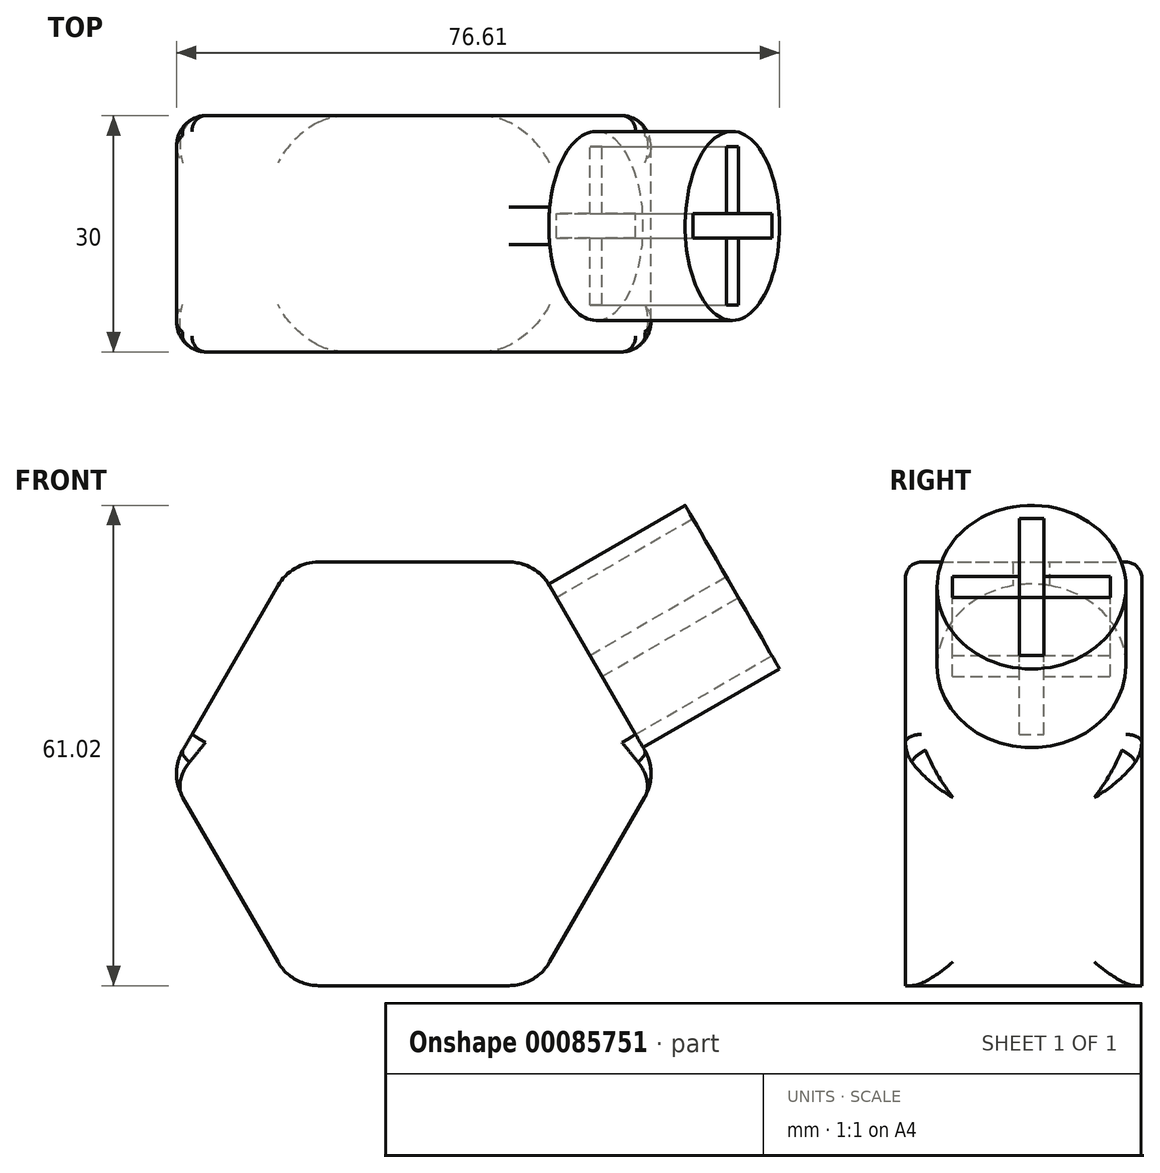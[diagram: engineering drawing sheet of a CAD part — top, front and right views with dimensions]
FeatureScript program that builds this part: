
annotation { "Feature Type Name" : "Feature", "Feature Type Description" : "" }
export const myFeature = defineFeature(function(context is Context, id is Id, definition is map)
    precondition{}
    {
        {
            var Q0;
            Q0=qCreatedBy(makeId("Front.planeOp"),FACE);
            var sketch = newSketch(context, id + "F0", { "sketchPlane" : qUnion([Q0])});
            skPoint(sketch, "E0", {"position": v(0.1, 0) * mm});
            skCircle(sketch, "E1", {"center": v(0.1, 0) * mm, "radius": 15 * mm});
            skCircle(sketch, "E2.cCircle", {"center": v(0, 0) * mm, "radius": 26.9 * mm, "construction": true});
            skLineSegment(sketch, "E2.0", {"start": v(15.53, 26.9) * mm, "end": v(31.07, 0) * mm});
            skLineSegment(sketch, "E2.1", {"start": v(31.07, 0) * mm, "end": v(15.53, -26.9) * mm});
            skLineSegment(sketch, "E2.2", {"start": v(15.53, -26.9) * mm, "end": v(-15.53, -26.9) * mm});
            skLineSegment(sketch, "E2.3", {"start": v(-15.53, -26.9) * mm, "end": v(-31.07, 0) * mm});
            skLineSegment(sketch, "E2.4", {"start": v(-31.07, 0) * mm, "end": v(-15.53, 26.9) * mm});
            skLineSegment(sketch, "E2.5", {"start": v(-15.53, 26.9) * mm, "end": v(15.53, 26.9) * mm});
            skPoint(sketch, "E2.0.midPoint", {"position": v(23.3, 13.45) * mm});
            skLineSegment(sketch, "E3", {"start": v(-38.32, 0) * mm, "end": v(0.1, 0) * mm});
            skLineSegment(sketch, "E4.left", {"start": v(-15.53, 26.9) * mm, "end": v(-15.53, 26.9) * mm});
            skLineSegment(sketch, "E4.right", {"start": v(15.53, 26.9) * mm, "end": v(15.53, 26.9) * mm});
            skLineSegment(sketch, "E5.right", {"start": v(15.53, 26.9) * mm, "end": v(-4.47, 26.9) * mm});
            skSolve(sketch);
        }
        {
            var Q0;
            Q0=makeQuery(id+"F0.imprint","IMPRINT",FACE,{"disambiguationData":[TD([[makeQuery(id+"F0.imprint","IMPRINT",EDGE,{"derivedFrom":sQuery(id+"F0.wireOp",EDGE,"E1")}),-1.0]])]});
            var Q1;
            Q1=makeQuery(id+"F0.imprint","IMPRINT",FACE,{"disambiguationData":[TD([[makeQuery(id+"F0.imprint","IMPRINT",EDGE,{"derivedFrom":sQuery(id+"F0.wireOp",EDGE,"E1")}),1.0]])]});
            extrude(context, id + "F1", {"entities" : qUnion([Q0, Q1]), "depth" : 30 * mm});
        }
        {
            var Q0;
            Q0=makeQuery(id+"F1.opExtrude","SWEPT_FACE",FACE,{"disambiguationData":[OSD([sQuery(id+"F0.wireOp",EDGE,"E2.0")])]});
            var sketch = newSketch(context, id + "F2", { "sketchPlane" : qUnion([Q0])});
            skCircle(sketch, "E6", {"center": v(-14, 0.3) * mm, "radius": 12 * mm});
            skSolve(sketch);
        }
        {
            var Q0;
            Q0 = qSketchRegion(id + "F2", true);
            extrude(context, id + "F3", {"entities" : qUnion([Q0]), "operationType" : NewBodyOperationType.ADD, "depth" : 20 * mm});
        }
        {
            var Q0;
            Q0=makeQuery(id+"F1.opExtrude","SWEPT_EDGE",EDGE,{"disambiguationData":[OSD([sQuery(id+"F0.wireOp",EDGE,"E2.0"),sQuery(id+"F0.wireOp",EDGE,"E5.right")])]});
            var Q1;
            Q1=makeQuery(id+"F1.opExtrude","SWEPT_EDGE",EDGE,{"disambiguationData":[OSD([sQuery(id+"F0.wireOp",EDGE,"E2.4"),sQuery(id+"F0.wireOp",EDGE,"E2.5")])]});
            var Q2;
            Q2=makeQuery(id+"F1.opExtrude","SWEPT_EDGE",EDGE,{"disambiguationData":[OSD([sQuery(id+"F0.wireOp",EDGE,"E2.3"),sQuery(id+"F0.wireOp",EDGE,"E2.4")])]});
            var Q3;
            Q3=makeQuery(id+"F1.opExtrude","SWEPT_EDGE",EDGE,{"disambiguationData":[OSD([sQuery(id+"F0.wireOp",EDGE,"E2.2"),sQuery(id+"F0.wireOp",EDGE,"E2.3")])]});
            var Q4;
            Q4=makeQuery(id+"F1.opExtrude","SWEPT_EDGE",EDGE,{"disambiguationData":[OSD([sQuery(id+"F0.wireOp",EDGE,"E2.1"),sQuery(id+"F0.wireOp",EDGE,"E2.2")])]});
            var Q5;
            Q5=makeQuery(id+"F1.opExtrude","SWEPT_EDGE",EDGE,{"disambiguationData":[OSD([sQuery(id+"F0.wireOp",EDGE,"E2.0"),sQuery(id+"F0.wireOp",EDGE,"E2.1")])]});
            var Q6;
            Q6=makeQuery(id+"F1.opExtrude","CAP_EDGE",EDGE,{"disambiguationData":[OSD([sQuery(id+"F0.wireOp",EDGE,"E2.5"),sQuery(id+"F0.wireOp",EDGE,"E5.right")])],"isStart":false});
            var Q7;
            Q7=makeQuery(id+"F1.opExtrude","CAP_EDGE",EDGE,{"disambiguationData":[OSD([sQuery(id+"F0.wireOp",EDGE,"E2.3")])],"isStart":false});
            var Q8;
            Q8=makeQuery(id+"F1.opExtrude","CAP_EDGE",EDGE,{"disambiguationData":[OSD([sQuery(id+"F0.wireOp",EDGE,"E2.1")])],"isStart":false});
            var Q9;
            Q9=makeQuery(id+"F1.opExtrude","CAP_EDGE",EDGE,{"disambiguationData":[OSD([sQuery(id+"F0.wireOp",EDGE,"E2.5"),sQuery(id+"F0.wireOp",EDGE,"E5.right")])],"isStart":true});
            var Q10;
            Q10=makeQuery(id+"F1.opExtrude","CAP_EDGE",EDGE,{"disambiguationData":[OSD([sQuery(id+"F0.wireOp",EDGE,"E2.3")])],"isStart":true});
            var Q11;
            Q11=makeQuery(id+"F1.opExtrude","CAP_EDGE",EDGE,{"disambiguationData":[OSD([sQuery(id+"F0.wireOp",EDGE,"E2.1")])],"isStart":true});
            fillet(context, id + "F4", {"entities" : qUnion([Q0, Q1, Q2, Q3, Q4, Q5, Q6, Q7, Q8, Q9, Q10, Q11]), "radius" : 6 * mm, "tangentPropagation" : true, "allowEdgeOverflow" : false});
        }
        {
            var Q0;
            Q0=makeQuery(id+"F1.opExtrude","CAP_EDGE",EDGE,{"disambiguationData":[OSD([sQuery(id+"F0.wireOp",EDGE,"E2.0")])],"isStart":true});
            var Q1;
            Q1=makeQuery(id+"F1.opExtrude","CAP_EDGE",EDGE,{"disambiguationData":[OSD([sQuery(id+"F0.wireOp",EDGE,"E2.0")])],"isStart":false});
            fillet(context, id + "F5", {"entities" : qUnion([Q0, Q1]), "radius" : 2 * mm, "tangentPropagation" : true, "allowEdgeOverflow" : false});
        }
        {
            var Q0;
            Q0=makeQuery(id+"F3.opExtrude","CAP_FACE",FACE,{"disambiguationData":[OSD([sQuery(id+"F2.wireOp",EDGE,"E6")])],"isStart":false});
            var sketch = newSketch(context, id + "F6", { "sketchPlane" : qUnion([Q0])});
            skLineSegment(sketch, "E7.bottom", {"start": v(-53.6, -77.57) * mm, "end": v(-60.22, -77.57) * mm});
            skLineSegment(sketch, "E7.top", {"start": v(-53.6, -67.04) * mm, "end": v(-60.22, -67.04) * mm});
            skLineSegment(sketch, "E7.left", {"start": v(-53.6, -77.57) * mm, "end": v(-53.6, -67.04) * mm});
            skLineSegment(sketch, "E7.right", {"start": v(-60.22, -77.57) * mm, "end": v(-60.22, -67.04) * mm});
            skLineSegment(sketch, "E8.left", {"start": v(-25.97, 0.3) * mm, "end": v(-25.97, 0.3) * mm});
            skLineSegment(sketch, "E8.right", {"start": v(-2.03, 0.3) * mm, "end": v(-2.03, 0.3) * mm});
            skPoint(sketch, "E8.middle", {"position": v(-14, 0.3) * mm});
            skLineSegment(sketch, "E9.bottom", {"start": v(-15.55, -9.74) * mm, "end": v(-12.45, -9.74) * mm});
            skLineSegment(sketch, "E9.top", {"start": v(-15.55, 10.36) * mm, "end": v(-12.45, 10.36) * mm});
            skLineSegment(sketch, "E9.left", {"start": v(-15.55, -9.74) * mm, "end": v(-15.55, -1.24) * mm});
            skLineSegment(sketch, "E9.right", {"start": v(-12.45, -9.74) * mm, "end": v(-12.45, -1.24) * mm});
            skLineSegment(sketch, "E10.bottom", {"start": v(-24.05, -1.24) * mm, "end": v(-15.55, -1.24) * mm});
            skLineSegment(sketch, "E10.top", {"start": v(-24.05, 1.86) * mm, "end": v(-15.55, 1.86) * mm});
            skLineSegment(sketch, "E10.left", {"start": v(-24.05, -1.24) * mm, "end": v(-24.05, 1.86) * mm});
            skLineSegment(sketch, "E10.right", {"start": v(-3.95, -1.24) * mm, "end": v(-3.95, 1.86) * mm});
            skLineSegment(sketch, "E11.trimOffspring", {"start": v(-12.45, -1.24) * mm, "end": v(-3.95, -1.24) * mm});
            skLineSegment(sketch, "E12.trimOffspring", {"start": v(-12.45, 1.86) * mm, "end": v(-12.45, 10.36) * mm});
            skLineSegment(sketch, "E13.trimOffspring", {"start": v(-12.45, 1.86) * mm, "end": v(-3.95, 1.86) * mm});
            skLineSegment(sketch, "E14.trimOffspring", {"start": v(-15.55, 1.86) * mm, "end": v(-15.55, 10.36) * mm});
            skSolve(sketch);
        }
        {
            var Q0;
            Q0 = qSketchRegion(id + "F6", true);
            extrude(context, id + "F7", {"entities" : qUnion([Q0]), "operationType" : NewBodyOperationType.REMOVE, "oppositeDirection" : true, "depth" : 20 * mm});
        }
    });
